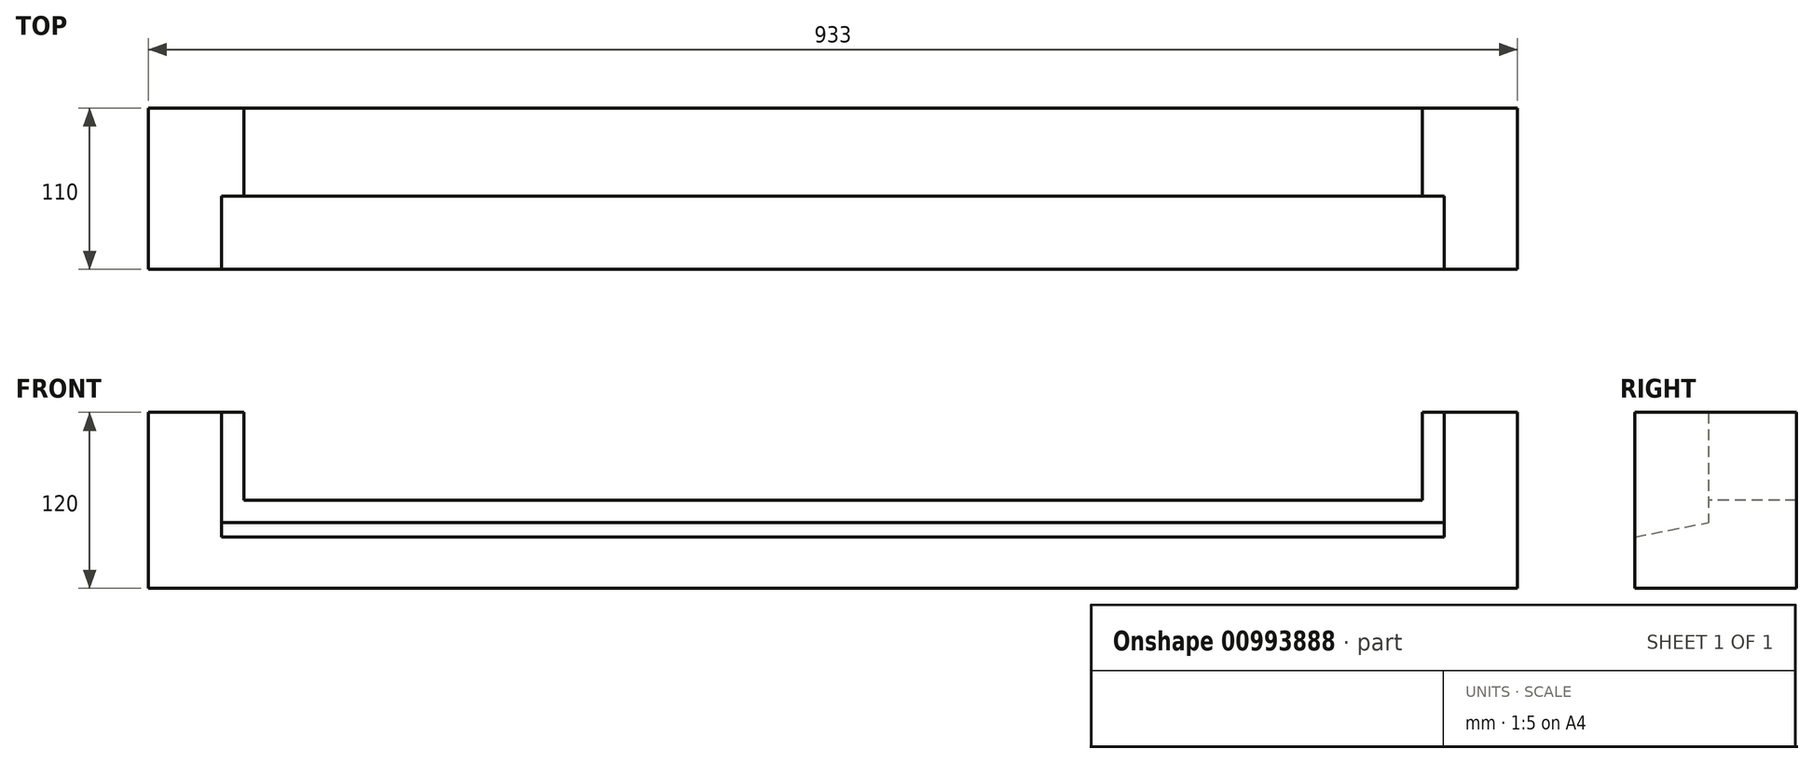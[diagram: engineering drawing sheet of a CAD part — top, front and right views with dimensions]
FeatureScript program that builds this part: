
annotation { "Feature Type Name" : "Feature", "Feature Type Description" : "" }
export const myFeature = defineFeature(function(context is Context, id is Id, definition is map)
    precondition{}
    {
        {
            var Q0;
            Q0=qCreatedBy(makeId("Right.planeOp"),FACE);
            var sketch = newSketch(context, id + "F0", { "sketchPlane" : qUnion([Q0])});
            skLineSegment(sketch, "E0", {"start": v(-55, 0) * mm, "end": v(55, 0) * mm});
            skLineSegment(sketch, "E1", {"start": v(55, 0) * mm, "end": v(55, 60) * mm});
            skLineSegment(sketch, "E2", {"start": v(55, 60) * mm, "end": v(-5, 60) * mm});
            skLineSegment(sketch, "E3", {"start": v(-5, 60) * mm, "end": v(-5, 45) * mm});
            skLineSegment(sketch, "E4", {"start": v(-55, 0) * mm, "end": v(-55, 35) * mm});
            skLineSegment(sketch, "E5", {"start": v(-55, 35) * mm, "end": v(-5, 45) * mm});
            skSolve(sketch);
        }
        {
            var Q0;
            Q0=makeQuery(id+"F0.imprint","IMPRINT",FACE,{"disambiguationData":[TD([[makeQuery(id+"F0.imprint","IMPRINT",EDGE,{"derivedFrom":sQuery(id+"F0.wireOp",EDGE,"E0")}),1.0]])]});
            extrude(context, id + "F1", {"entities" : qUnion([Q0]), "endBound" : BoundingType.SYMMETRIC, "depth" : 933 * mm, "offsetDistance" : 25 * mm});
        }
        {
            var Q0;
            Q0=makeQuery(id+"F1.opExtrude","SWEPT_FACE",FACE,{"disambiguationData":[OSD([sQuery(id+"F0.wireOp",EDGE,"E0")])]});
            var sketch = newSketch(context, id + "F2", { "sketchPlane" : qUnion([Q0])});
            skLineSegment(sketch, "E6", {"start": v(466.5, 55) * mm, "end": v(466.5, -55) * mm});
            skLineSegment(sketch, "E7", {"start": v(466.5, -55) * mm, "end": v(401.5, -55) * mm});
            skLineSegment(sketch, "E8", {"start": v(401.5, -55) * mm, "end": v(401.5, 5) * mm});
            skLineSegment(sketch, "E9", {"start": v(401.5, 5) * mm, "end": v(416.5, 5) * mm});
            skLineSegment(sketch, "E10", {"start": v(416.5, 5) * mm, "end": v(416.5, 55) * mm});
            skLineSegment(sketch, "E11", {"start": v(416.5, 55) * mm, "end": v(466.5, 55) * mm});
            skLineSegment(sketch, "E12.MirrorCS", {"start": v(-416.5, 55) * mm, "end": v(-466.5, 55) * mm});
            skLineSegment(sketch, "E13.MirrorCS", {"start": v(-416.5, 5) * mm, "end": v(-416.5, 55) * mm});
            skLineSegment(sketch, "E14.MirrorCS", {"start": v(-401.5, 5) * mm, "end": v(-416.5, 5) * mm});
            skLineSegment(sketch, "E15.MirrorCS", {"start": v(-401.5, -55) * mm, "end": v(-401.5, 5) * mm});
            skLineSegment(sketch, "E16.MirrorCS", {"start": v(-466.5, -55) * mm, "end": v(-401.5, -55) * mm});
            skLineSegment(sketch, "E17.MirrorCS", {"start": v(-466.5, 55) * mm, "end": v(-466.5, -55) * mm});
            skSolve(sketch);
        }
        {
            var Q0;
            Q0=makeQuery(id+"F2.imprint","IMPRINT",FACE,{"disambiguationData":[TD([[makeQuery(id+"F2.imprint","IMPRINT",EDGE,{"derivedFrom":sQuery(id+"F2.wireOp",EDGE,"E12.MirrorCS")}),1.0]])]});
            var Q1;
            Q1=makeQuery(id+"F2.imprint","IMPRINT",FACE,{"disambiguationData":[TD([[makeQuery(id+"F2.imprint","IMPRINT",EDGE,{"derivedFrom":sQuery(id+"F2.wireOp",EDGE,"E6")}),-1.0]])]});
            extrude(context, id + "F3", {"entities" : qUnion([Q0, Q1]), "operationType" : NewBodyOperationType.ADD, "oppositeDirection" : true, "depth" : 120 * mm, "offsetDistance" : 25 * mm});
        }
    });
